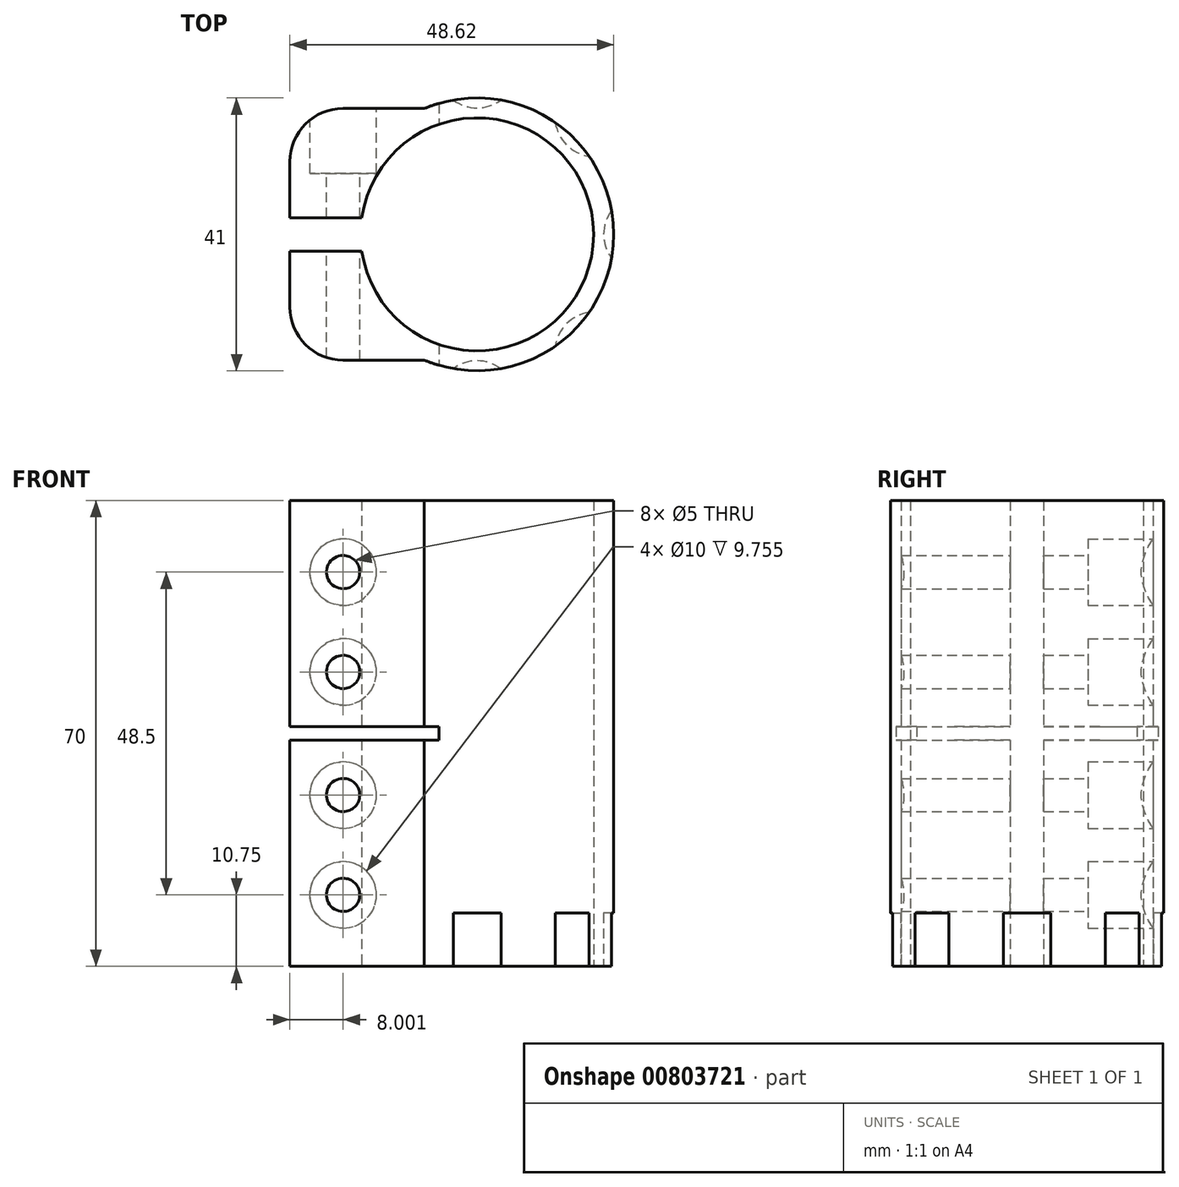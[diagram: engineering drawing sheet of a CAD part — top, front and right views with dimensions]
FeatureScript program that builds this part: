
annotation { "Feature Type Name" : "Feature", "Feature Type Description" : "" }
export const myFeature = defineFeature(function(context is Context, id is Id, definition is map)
    precondition{}
    {
        {
            var Q0;
            Q0=qCreatedBy(makeId("Top.planeOp"),FACE);
            var sketch = newSketch(context, id + "F0", { "sketchPlane" : qUnion([Q0])});
            skArc(sketch, "E0", {"start": v(-17.32, -2.5) * mm, "mid": v(17.5, 0) * mm, "end": v(-17.32, 2.5) * mm});
            skArc(sketch, "E1", {"start": v(-7.92, -18.9) * mm, "mid": v(20.5, 0) * mm, "end": v(-7.92, 18.9) * mm});
            skLineSegment(sketch, "E2", {"start": v(-17.32, 2.5) * mm, "end": v(-28.12, 2.5) * mm});
            skLineSegment(sketch, "E3", {"start": v(-28.12, 2.5) * mm, "end": v(-28.12, 10.9) * mm});
            skLineSegment(sketch, "E4", {"start": v(-20.12, 18.9) * mm, "end": v(-7.92, 18.9) * mm});
            skPoint(sketch, "E5.visualSharp", {"position": v(-28.12, 18.9) * mm});
            skArc(sketch, "E5.filletArc", {"start": v(-20.12, 18.9) * mm, "mid": v(-25.78, 16.57) * mm, "end": v(-28.12, 10.9) * mm});
            skLineSegment(sketch, "E6", {"start": v(0, 0) * mm, "end": v(33.02, 0) * mm, "construction": true});
            skLineSegment(sketch, "E7.MirrorCS", {"start": v(-20.12, -18.9) * mm, "end": v(-7.92, -18.9) * mm});
            skArc(sketch, "E8.MirrorCS", {"start": v(-20.12, -18.9) * mm, "mid": v(-25.78, -16.57) * mm, "end": v(-28.12, -10.9) * mm});
            skLineSegment(sketch, "E9.MirrorCS", {"start": v(-28.12, -2.5) * mm, "end": v(-28.12, -10.9) * mm});
            skLineSegment(sketch, "E10.MirrorCS", {"start": v(-17.32, -2.5) * mm, "end": v(-28.12, -2.5) * mm});
            skSolve(sketch);
        }
        {
            var Q0;
            Q0=makeQuery(id+"F0.imprint","IMPRINT",FACE,{"disambiguationData":[TD([[makeQuery(id+"F0.imprint","IMPRINT",EDGE,{"derivedFrom":sQuery(id+"F0.wireOp",EDGE,"E0")}),-1.0]])]});
            extrude(context, id + "F1", {"entities" : qUnion([Q0]), "endBound" : BoundingType.SYMMETRIC, "depth" : 70 * mm, "offsetDistance" : 25 * mm});
        }
        {
            var Q0;
            Q0=makeQuery(id+"F1.opExtrude","SWEPT_FACE",FACE,{"disambiguationData":[OSD([sQuery(id+"F0.wireOp",EDGE,"E4")])]});
            var sketch = newSketch(context, id + "F2", { "sketchPlane" : qUnion([Q0])});
            skPoint(sketch, "E11", {"position": v(20.12, -24.25) * mm});
            skPoint(sketch, "E12", {"position": v(20.12, -9.25) * mm});
            skPoint(sketch, "E13", {"position": v(20.12, 9.25) * mm});
            skPoint(sketch, "E14", {"position": v(20.12, 24.25) * mm});
            skSolve(sketch);
        }
        {
            var Q0;
            Q0=sQuery(id+"F2.wireOp",VERTEX,"E11");
            var Q1;
            Q1=sQuery(id+"F2.wireOp",VERTEX,"E12");
            var Q2;
            Q2=sQuery(id+"F2.wireOp",VERTEX,"E13");
            var Q3;
            Q3=sQuery(id+"F2.wireOp",VERTEX,"E14");
            var Q4;
            Q4=makeQuery(id+"F1.opExtrude","SWEPT_BODY",BODY,{"disambiguationData":[OSD([sQuery(id+"F0.wireOp",EDGE,"E0"),sQuery(id+"F0.wireOp",EDGE,"E1"),sQuery(id+"F0.wireOp",EDGE,"E2"),sQuery(id+"F0.wireOp",EDGE,"E3"),sQuery(id+"F0.wireOp",EDGE,"E4"),sQuery(id+"F0.wireOp",EDGE,"E5.filletArc"),sQuery(id+"F0.wireOp",EDGE,"E7.MirrorCS"),sQuery(id+"F0.wireOp",EDGE,"E8.MirrorCS"),sQuery(id+"F0.wireOp",EDGE,"E9.MirrorCS"),sQuery(id+"F0.wireOp",EDGE,"E10.MirrorCS")])]});
            hole(context, id + "F3", {"style" : HoleStyle.C_BORE, "endStyle" : HoleEndStyle.THROUGH, "holeDiameter" : 5 * mm, "cBoreDiameter" : 10 * mm, "cBoreDepth" : 8 * mm, "majorDiameter" : 5 * mm, "isTappedThrough" : true, "tappedDepth" : 12 * mm, "tapClearance" : 3, "locations" : qUnion([Q0, Q1, Q2, Q3]), "scope" : qUnion([Q4])});
        }
        {
            var Q0;
            Q0=qCreatedBy(makeId("Front.planeOp"),FACE);
            var sketch = newSketch(context, id + "F4", { "sketchPlane" : qUnion([Q0])});
            skLineSegment(sketch, "E15.bottom", {"start": v(-28.12, -1) * mm, "end": v(-5.72, -1) * mm});
            skLineSegment(sketch, "E15.top", {"start": v(-28.12, 1) * mm, "end": v(-5.72, 1) * mm});
            skLineSegment(sketch, "E15.left", {"start": v(-28.12, -1) * mm, "end": v(-28.12, 1) * mm});
            skLineSegment(sketch, "E15.right", {"start": v(-5.72, -1) * mm, "end": v(-5.72, 1) * mm});
            skSolve(sketch);
        }
        {
            var Q0;
            Q0=makeQuery(id+"F4.imprint","IMPRINT",FACE,{"disambiguationData":[TD([[makeQuery(id+"F4.imprint","IMPRINT",EDGE,{"derivedFrom":sQuery(id+"F4.wireOp",EDGE,"E15.bottom")}),1.0]])]});
            extrude(context, id + "F5", {"entities" : qUnion([Q0]), "operationType" : NewBodyOperationType.REMOVE, "endBound" : BoundingType.SYMMETRIC, "oppositeDirection" : true, "depth" : 50 * mm, "offsetDistance" : 25 * mm});
        }
        {
            var Q0;
            Q0=makeQuery(id+"F1.opExtrude","CAP_FACE",FACE,{"disambiguationData":[OSD([sQuery(id+"F0.wireOp",EDGE,"E0"),sQuery(id+"F0.wireOp",EDGE,"E1"),sQuery(id+"F0.wireOp",EDGE,"E2"),sQuery(id+"F0.wireOp",EDGE,"E3"),sQuery(id+"F0.wireOp",EDGE,"E4"),sQuery(id+"F0.wireOp",EDGE,"E5.filletArc"),sQuery(id+"F0.wireOp",EDGE,"E7.MirrorCS"),sQuery(id+"F0.wireOp",EDGE,"E8.MirrorCS"),sQuery(id+"F0.wireOp",EDGE,"E9.MirrorCS"),sQuery(id+"F0.wireOp",EDGE,"E10.MirrorCS")])],"isStart":true});
            var sketch = newSketch(context, id + "F6", { "sketchPlane" : qUnion([Q0])});
            skCircle(sketch, "E16", {"center": v(0, -25) * mm, "radius": 6 * mm});
            skCircle(sketch, "E17.1.0", {"center": v(17.68, -17.68) * mm, "radius": 6 * mm});
            skCircle(sketch, "E17.2.0", {"center": v(25, 0) * mm, "radius": 6 * mm});
            skCircle(sketch, "E17.3.0", {"center": v(17.68, 17.68) * mm, "radius": 6 * mm});
            skCircle(sketch, "E17.4.0", {"center": v(0, 25) * mm, "radius": 6 * mm});
            skPoint(sketch, "E17.center", {"position": v(0, 0) * mm});
            skLineSegment(sketch, "E17.anchor1", {"start": v(0, 0) * mm, "end": v(0, -25) * mm, "construction": true});
            skLineSegment(sketch, "E17.anchor2", {"start": v(0, 0) * mm, "end": v(0, 25) * mm, "construction": true});
            skSolve(sketch);
        }
        {
            var Q0;
            {var subQ0=sQuery(id+"F6.wireOp",EDGE,"E17.4.0");var subQ1=makeQuery(id+"F1.opExtrude","CAP_EDGE",EDGE,{"disambiguationData":[OSD([sQuery(id+"F0.wireOp",EDGE,"E1")])],"isStart":true});var subQ2=makeQuery(id+"F6.imprint","INTERSECT",VERTEX,{"disambiguationData":[OD(0.0)],"derivedFrom":[subQ1,subQ0]});Q0=makeQuery(id+"F6.imprint","IMPRINT",FACE,{"disambiguationData":[TD([[makeQuery(id+"F6.imprint","IMPRINT",EDGE,{"disambiguationData":[TD([[subQ2,1.0]])],"derivedFrom":subQ0}),1.0]])]});}
            var Q1;
            {var subQ0=sQuery(id+"F6.wireOp",EDGE,"E17.3.0");var subQ1=makeQuery(id+"F1.opExtrude","CAP_EDGE",EDGE,{"disambiguationData":[OSD([sQuery(id+"F0.wireOp",EDGE,"E1")])],"isStart":true});var subQ2=makeQuery(id+"F6.imprint","INTERSECT",VERTEX,{"disambiguationData":[OD(0.0)],"derivedFrom":[subQ1,subQ0]});Q1=makeQuery(id+"F6.imprint","IMPRINT",FACE,{"disambiguationData":[TD([[makeQuery(id+"F6.imprint","IMPRINT",EDGE,{"disambiguationData":[TD([[subQ2,1.0]])],"derivedFrom":subQ0}),1.0]])]});}
            var Q2;
            {var subQ0=sQuery(id+"F6.wireOp",EDGE,"E17.2.0");var subQ1=makeQuery(id+"F1.opExtrude","CAP_EDGE",EDGE,{"disambiguationData":[OSD([sQuery(id+"F0.wireOp",EDGE,"E1")])],"isStart":true});var subQ2=makeQuery(id+"F6.imprint","INTERSECT",VERTEX,{"disambiguationData":[OD(0.0)],"derivedFrom":[subQ1,subQ0]});Q2=makeQuery(id+"F6.imprint","IMPRINT",FACE,{"disambiguationData":[TD([[makeQuery(id+"F6.imprint","IMPRINT",EDGE,{"disambiguationData":[TD([[subQ2,-1.0]])],"derivedFrom":subQ0}),1.0]])]});}
            var Q3;
            {var subQ0=sQuery(id+"F6.wireOp",EDGE,"E17.1.0");var subQ1=makeQuery(id+"F1.opExtrude","CAP_EDGE",EDGE,{"disambiguationData":[OSD([sQuery(id+"F0.wireOp",EDGE,"E1")])],"isStart":true});var subQ2=makeQuery(id+"F6.imprint","INTERSECT",VERTEX,{"disambiguationData":[OD(0.0)],"derivedFrom":[subQ1,subQ0]});Q3=makeQuery(id+"F6.imprint","IMPRINT",FACE,{"disambiguationData":[TD([[makeQuery(id+"F6.imprint","IMPRINT",EDGE,{"disambiguationData":[TD([[subQ2,-1.0]])],"derivedFrom":subQ0}),1.0]])]});}
            var Q4;
            {var subQ0=sQuery(id+"F6.wireOp",EDGE,"E16");var subQ1=makeQuery(id+"F1.opExtrude","CAP_EDGE",EDGE,{"disambiguationData":[OSD([sQuery(id+"F0.wireOp",EDGE,"E1")])],"isStart":true});var subQ2=makeQuery(id+"F6.imprint","INTERSECT",VERTEX,{"disambiguationData":[OD(0.0)],"derivedFrom":[subQ1,subQ0]});Q4=makeQuery(id+"F6.imprint","IMPRINT",FACE,{"disambiguationData":[TD([[makeQuery(id+"F6.imprint","IMPRINT",EDGE,{"disambiguationData":[TD([[subQ2,-1.0]])],"derivedFrom":subQ0}),1.0]])]});}
            var Q5;
            {var subQ0=sQuery(id+"F6.wireOp",EDGE,"E17.4.0");var subQ1=makeQuery(id+"F1.opExtrude","CAP_EDGE",EDGE,{"disambiguationData":[OSD([sQuery(id+"F0.wireOp",EDGE,"E1")])],"isStart":true});var subQ2=makeQuery(id+"F6.imprint","INTERSECT",VERTEX,{"disambiguationData":[OD(0.0)],"derivedFrom":[subQ1,subQ0]});Q5=makeQuery(id+"F6.imprint","IMPRINT",FACE,{"disambiguationData":[TD([[makeQuery(id+"F6.imprint","IMPRINT",EDGE,{"disambiguationData":[TD([[subQ2,-1.0]])],"derivedFrom":subQ0}),1.0]])]});}
            var Q6;
            {var subQ0=sQuery(id+"F6.wireOp",EDGE,"E17.3.0");var subQ1=makeQuery(id+"F1.opExtrude","CAP_EDGE",EDGE,{"disambiguationData":[OSD([sQuery(id+"F0.wireOp",EDGE,"E1")])],"isStart":true});var subQ2=makeQuery(id+"F6.imprint","INTERSECT",VERTEX,{"disambiguationData":[OD(0.0)],"derivedFrom":[subQ1,subQ0]});Q6=makeQuery(id+"F6.imprint","IMPRINT",FACE,{"disambiguationData":[TD([[makeQuery(id+"F6.imprint","IMPRINT",EDGE,{"disambiguationData":[TD([[subQ2,-1.0]])],"derivedFrom":subQ0}),1.0]])]});}
            var Q7;
            {var subQ0=sQuery(id+"F6.wireOp",EDGE,"E17.2.0");var subQ1=makeQuery(id+"F1.opExtrude","CAP_EDGE",EDGE,{"disambiguationData":[OSD([sQuery(id+"F0.wireOp",EDGE,"E1")])],"isStart":true});var subQ2=makeQuery(id+"F6.imprint","INTERSECT",VERTEX,{"disambiguationData":[OD(0.0)],"derivedFrom":[subQ1,subQ0]});Q7=makeQuery(id+"F6.imprint","IMPRINT",FACE,{"disambiguationData":[TD([[makeQuery(id+"F6.imprint","IMPRINT",EDGE,{"disambiguationData":[TD([[subQ2,1.0]])],"derivedFrom":subQ0}),1.0]])]});}
            var Q8;
            {var subQ0=sQuery(id+"F6.wireOp",EDGE,"E17.1.0");var subQ1=makeQuery(id+"F1.opExtrude","CAP_EDGE",EDGE,{"disambiguationData":[OSD([sQuery(id+"F0.wireOp",EDGE,"E1")])],"isStart":true});var subQ2=makeQuery(id+"F6.imprint","INTERSECT",VERTEX,{"disambiguationData":[OD(0.0)],"derivedFrom":[subQ1,subQ0]});Q8=makeQuery(id+"F6.imprint","IMPRINT",FACE,{"disambiguationData":[TD([[makeQuery(id+"F6.imprint","IMPRINT",EDGE,{"disambiguationData":[TD([[subQ2,1.0]])],"derivedFrom":subQ0}),1.0]])]});}
            var Q9;
            {var subQ0=sQuery(id+"F6.wireOp",EDGE,"E16");var subQ1=makeQuery(id+"F1.opExtrude","CAP_EDGE",EDGE,{"disambiguationData":[OSD([sQuery(id+"F0.wireOp",EDGE,"E1")])],"isStart":true});var subQ2=makeQuery(id+"F6.imprint","INTERSECT",VERTEX,{"disambiguationData":[OD(0.0)],"derivedFrom":[subQ1,subQ0]});Q9=makeQuery(id+"F6.imprint","IMPRINT",FACE,{"disambiguationData":[TD([[makeQuery(id+"F6.imprint","IMPRINT",EDGE,{"disambiguationData":[TD([[subQ2,1.0]])],"derivedFrom":subQ0}),1.0]])]});}
            extrude(context, id + "F7", {"entities" : qUnion([Q0, Q1, Q2, Q3, Q4, Q5, Q6, Q7, Q8, Q9]), "operationType" : NewBodyOperationType.REMOVE, "oppositeDirection" : true, "depth" : 8 * mm, "offsetDistance" : 25 * mm});
        }
    });
